# Revit family: Urinal-Wall_Mount_High_Efficiency-KOHLER-Bardon-K-4991
name_source: partatom
category: Plumbing Fixtures
revit_build: Autodesk Revit 2015 (Build: 20140606_1530(x64)
units: mm (PartAtom-declared; Revit-internal decimal feet)

## types (5) — shared parameters
ADA Compliant = Yes
Assembly Code = D2010200
CW Connection = Yes
Cold Water Inlet = Cold Water Inlet
Date Modified = 11/1/2017
Default Elevation = 21"
Flow Rate = 0 GPM
Flush Rate = 1.0 GPF
HW Connection = No
Height = 14 3/16"
Hot Water Inlet = Hot Water Inlet
Length = 28 1/4"
Manufacturer = KOHLER Co.
MasterFormat 1995 = 15410
MasterFormat 2004 = 22.41.13
Material = Vitreous China
Pressure = 0.00 psi
Product Documentation Link = http://www.us.kohler.com
Product Name = Bardon
Product Page URL = http://www.us.kohler.com
Rough-In = 0"
URL = https://www.us.kohler.com
Vent Connection = No
Waste Connection = Yes
Waste Water Outlet = Waste Water Outlet
Width = 18 1/2"

## per-type parameters (varying)
| type | Connection | Constraint | Description | Finish | Model | Rear Spud | Top Spud | Type |
| Rear Spud-0-White | 0.00° | 1 | High-Efficiency Urinal (HEU), washdown, wall-hung, 0.125 gpf to 1.0 gpf, rear spud | Kohler-Vitreous_China-0-White | K-4991-ER-0 | Yes | No | 1 |
| Top Spud-0-White | 90.00° | 2 | High-Efficiency Urinal (HEU), Washdown, wall-hung, 0.125 gpf to 1.0 gpf, top spud | Kohler-Vitreous_China-0-White | K-4991-ET-0 | No | Yes | 1 |
| Top Spud-96-Biscuit | 90.00° | 2 | High-Efficiency Urinal (HEU), Washdown, wall-hung, 0.125 gpf to 1.0 gpf, top spud | Kohler-Vitreous_China-96-Biscuit | K-4991-ET-96 | No | Yes | 4 |
| Top Spud-47-Almond | 90.00° | 2 | High-Efficiency Urinal (HEU), Washdown, wall-hung, 0.125 gpf to 1.0 gpf, top spud | Kohler-Vitreous_China-47-Almond | K-4991-ET-47 | No | Yes | 2 |
| Top Spud-7-Black Black | 90.00° | 2 | High-Efficiency Urinal (HEU), Washdown, wall-hung, 0.125 gpf to 1.0 gpf, top spud | Kohler-Vitreous_China-7-Black_Black | K-4991-ET-7 | No | Yes | 3 |

## geometry (parser evidence)
native form markers: Blend x2, Sweep x5
no freeform markers — native parametric forms only
